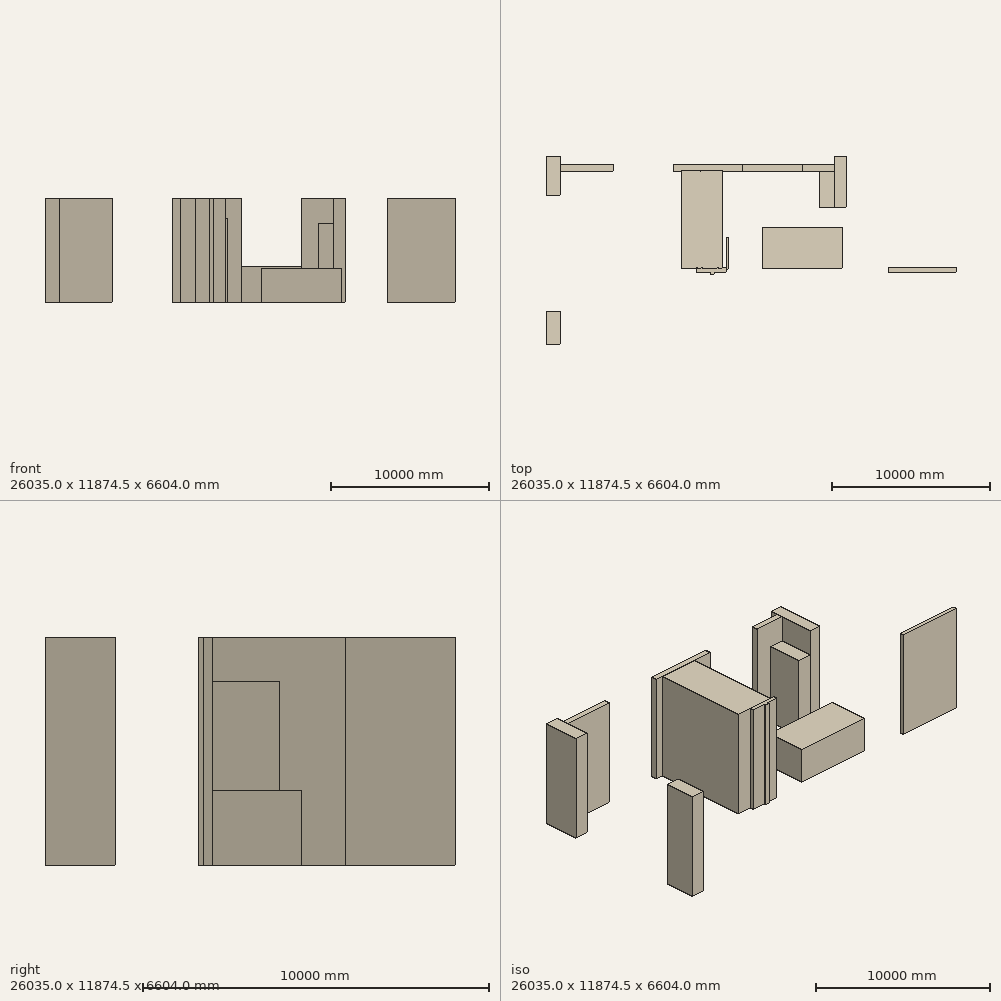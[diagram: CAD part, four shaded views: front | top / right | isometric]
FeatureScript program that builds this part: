
annotation { "Feature Type Name" : "Feature", "Feature Type Description" : "" }
export const myFeature = defineFeature(function(context is Context, id is Id, definition is map)
    precondition{}
    {
        {
            var Q0;
            Q0=qCreatedBy(makeId("Top.planeOp"),FACE);
            var sketch = newSketch(context, id + "F0", { "sketchPlane" : qUnion([Q0])});
            skLineSegment(sketch, "E0.bottom", {"start": v(0, 0) * mm, "end": v(762, 0) * mm});
            skLineSegment(sketch, "E0.top", {"start": v(0, -3175) * mm, "end": v(762, -3175) * mm});
            skLineSegment(sketch, "E0.left", {"start": v(0, 0) * mm, "end": v(0, -3175) * mm});
            skLineSegment(sketch, "E0.right", {"start": v(762, 0) * mm, "end": v(762, -3175) * mm});
            skLineSegment(sketch, "E1.bottom", {"start": v(0, -508) * mm, "end": v(-17399, -508) * mm});
            skLineSegment(sketch, "E1.top", {"start": v(0, -889) * mm, "end": v(-431.8, -889) * mm});
            skLineSegment(sketch, "E1.left", {"start": v(0, -508) * mm, "end": v(0, -889) * mm});
            skLineSegment(sketch, "E1.right", {"start": v(-17399, -508) * mm, "end": v(-17399, -889) * mm});
            skLineSegment(sketch, "E2.bottom", {"start": v(762, -3175) * mm, "end": v(508, -3175) * mm});
            skLineSegment(sketch, "E2.top", {"start": v(762, -7048.5) * mm, "end": v(508, -7048.5) * mm});
            skLineSegment(sketch, "E2.left", {"start": v(762, -3175) * mm, "end": v(762, -7048.5) * mm});
            skLineSegment(sketch, "E2.right", {"start": v(508, -4762.5) * mm, "end": v(508, -7048.5) * mm});
            skLineSegment(sketch, "E3.bottom", {"start": v(-17399, 0) * mm, "end": v(-18288, 0) * mm});
            skLineSegment(sketch, "E3.top", {"start": v(-17399, -2413) * mm, "end": v(-18288, -2413) * mm});
            skLineSegment(sketch, "E3.left", {"start": v(-17399, 0) * mm, "end": v(-17399, -2413) * mm});
            skLineSegment(sketch, "E3.right", {"start": v(-18288, 0) * mm, "end": v(-18288, -2413) * mm});
            skLineSegment(sketch, "E4.bottom", {"start": v(-18288, -2413) * mm, "end": v(-17907, -2413) * mm});
            skLineSegment(sketch, "E4.top", {"start": v(-18288, -9842.5) * mm, "end": v(-17907, -9842.5) * mm});
            skLineSegment(sketch, "E4.left", {"start": v(-18288, -2413) * mm, "end": v(-18288, -9842.5) * mm});
            skLineSegment(sketch, "E4.right", {"start": v(-17907, -2413) * mm, "end": v(-17907, -9842.5) * mm});
            skLineSegment(sketch, "E5.bottom", {"start": v(-18288, -9842.5) * mm, "end": v(-17399, -9842.5) * mm});
            skLineSegment(sketch, "E5.top", {"start": v(-18288, -11874.5) * mm, "end": v(-17399, -11874.5) * mm});
            skLineSegment(sketch, "E5.left", {"start": v(-18288, -9842.5) * mm, "end": v(-18288, -11874.5) * mm});
            skLineSegment(sketch, "E5.right", {"start": v(-17399, -9842.5) * mm, "end": v(-17399, -11874.5) * mm});
            skLineSegment(sketch, "E6.bottom", {"start": v(-7614.3, -7048.5) * mm, "end": v(7747, -7048.5) * mm});
            skLineSegment(sketch, "E6.top", {"start": v(-7614.3, -7302.5) * mm, "end": v(7747, -7302.5) * mm});
            skLineSegment(sketch, "E6.right", {"start": v(7747, -7048.5) * mm, "end": v(7747, -7302.5) * mm});
            skLineSegment(sketch, "E7.top", {"start": v(-7614.3, -9842.5) * mm, "end": v(7747, -9842.5) * mm});
            skLineSegment(sketch, "E7.left", {"start": v(-7614.3, -7302.5) * mm, "end": v(-7614.3, -9842.5) * mm});
            skLineSegment(sketch, "E7.right", {"start": v(7747, -7302.5) * mm, "end": v(7747, -9842.5) * mm});
            skLineSegment(sketch, "E8.bottom", {"start": v(-5588, -9842.5) * mm, "end": v(1016, -9842.5) * mm});
            skLineSegment(sketch, "E8.top", {"start": v(-4826, -10604.5) * mm, "end": v(1016, -10604.5) * mm});
            skLineSegment(sketch, "E8.left", {"start": v(-5588, -9842.5) * mm, "end": v(-5588, -10604.5) * mm});
            skLineSegment(sketch, "E8.right", {"start": v(1016, -9842.5) * mm, "end": v(1016, -10604.5) * mm});
            skLineSegment(sketch, "E9.top", {"start": v(-5588, -15303.5) * mm, "end": v(-4826, -15303.5) * mm});
            skLineSegment(sketch, "E9.left", {"start": v(-5588, -10604.5) * mm, "end": v(-5588, -15303.5) * mm});
            skLineSegment(sketch, "E9.right", {"start": v(-4826, -10604.5) * mm, "end": v(-4826, -15303.5) * mm});
            skLineSegment(sketch, "E10", {"start": v(-5588, -9842.5) * mm, "end": v(-17907, -9842.5) * mm});
            skLineSegment(sketch, "E11.top", {"start": v(-5588, -10096.5) * mm, "end": v(-7874, -10096.5) * mm});
            skLineSegment(sketch, "E11.left", {"start": v(-5588, -9842.5) * mm, "end": v(-5588, -10096.5) * mm});
            skLineSegment(sketch, "E12.bottom", {"start": v(-17907, -9842.5) * mm, "end": v(-7874, -9842.5) * mm});
            skLineSegment(sketch, "E12.top", {"start": v(-17907, -9588.5) * mm, "end": v(-7874, -9588.5) * mm});
            skLineSegment(sketch, "E12.left", {"start": v(-17907, -9842.5) * mm, "end": v(-17907, -9588.5) * mm});
            skLineSegment(sketch, "E12.right", {"start": v(-7874, -9842.5) * mm, "end": v(-7874, -9588.5) * mm});
            skLineSegment(sketch, "E13.bottom", {"start": v(-5588, -10096.5) * mm, "end": v(-5842, -10096.5) * mm});
            skLineSegment(sketch, "E13.top", {"start": v(-5588, -9842.5) * mm, "end": v(-5842, -9842.5) * mm});
            skLineSegment(sketch, "E13.left", {"start": v(-5588, -10096.5) * mm, "end": v(-5588, -9842.5) * mm});
            skLineSegment(sketch, "E13.right", {"start": v(-5842, -10096.5) * mm, "end": v(-5842, -9842.5) * mm});
            skLineSegment(sketch, "E14.bottom", {"start": v(-5842, -9842.5) * mm, "end": v(-7620, -9842.5) * mm});
            skLineSegment(sketch, "E14.top", {"start": v(-5842, -10096.5) * mm, "end": v(-7620, -10096.5) * mm});
            skLineSegment(sketch, "E14.left", {"start": v(-5842, -9842.5) * mm, "end": v(-5842, -10096.5) * mm});
            skLineSegment(sketch, "E14.right", {"start": v(-7620, -9842.5) * mm, "end": v(-7620, -10096.5) * mm});
            skLineSegment(sketch, "E15.bottom", {"start": v(-7620, -9842.5) * mm, "end": v(-7874, -9842.5) * mm});
            skLineSegment(sketch, "E15.top", {"start": v(-7620, -10096.5) * mm, "end": v(-7874, -10096.5) * mm});
            skLineSegment(sketch, "E15.right", {"start": v(-7874, -9842.5) * mm, "end": v(-7874, -10096.5) * mm});
            skLineSegment(sketch, "E16.bottom", {"start": v(-7874, -9842.5) * mm, "end": v(-7614.3, -9842.5) * mm});
            skLineSegment(sketch, "E16.top", {"start": v(-7874, -9461.5) * mm, "end": v(-7614.3, -9461.5) * mm});
            skLineSegment(sketch, "E16.left", {"start": v(-7874, -9842.5) * mm, "end": v(-7874, -9461.5) * mm});
            skLineSegment(sketch, "E16.right", {"start": v(-7614.3, -9842.5) * mm, "end": v(-7614.3, -9461.5) * mm});
            skLineSegment(sketch, "E17.left", {"start": v(-7874, -9461.5) * mm, "end": v(-7874, -7302.5) * mm});
            skLineSegment(sketch, "E17.right", {"start": v(-7614.3, -9461.5) * mm, "end": v(-7614.3, -7302.5) * mm});
            skLineSegment(sketch, "E18.top", {"start": v(-7874, -7429.5) * mm, "end": v(-7614.3, -7429.5) * mm});
            skLineSegment(sketch, "E18.left", {"start": v(-7874, -7302.5) * mm, "end": v(-7874, -7429.5) * mm});
            skLineSegment(sketch, "E18.right", {"start": v(-7614.3, -7302.5) * mm, "end": v(-7614.3, -7429.5) * mm});
            skLineSegment(sketch, "E19.bottom", {"start": v(-14033.5, -508) * mm, "end": v(-10223.5, -508) * mm});
            skLineSegment(sketch, "E19.top", {"start": v(-14033.5, -889) * mm, "end": v(-10223.5, -889) * mm});
            skLineSegment(sketch, "E19.left", {"start": v(-14033.5, -508) * mm, "end": v(-14033.5, -889) * mm});
            skLineSegment(sketch, "E19.right", {"start": v(-10223.5, -508) * mm, "end": v(-10223.5, -889) * mm});
            skLineSegment(sketch, "E20.bottom", {"start": v(-5842, -508) * mm, "end": v(-2032, -508) * mm});
            skLineSegment(sketch, "E20.top", {"start": v(-5842, -889) * mm, "end": v(-5080, -889) * mm});
            skLineSegment(sketch, "E20.left", {"start": v(-5842, -508) * mm, "end": v(-5842, -889) * mm});
            skLineSegment(sketch, "E20.right", {"start": v(-2032, -508) * mm, "end": v(-2032, -889) * mm});
            skLineSegment(sketch, "E21.bottom", {"start": v(-9715.5, -889) * mm, "end": v(-7106.3, -889) * mm});
            skLineSegment(sketch, "E21.top", {"start": v(-9715.5, -7048.5) * mm, "end": v(-7106.3, -7048.5) * mm});
            skLineSegment(sketch, "E21.left", {"start": v(-9715.5, -889) * mm, "end": v(-9715.5, -7048.5) * mm});
            skLineSegment(sketch, "E21.right", {"start": v(-7106.3, -889) * mm, "end": v(-7106.3, -7048.5) * mm});
            skLineSegment(sketch, "E22.bottom", {"start": v(-7874, -7302.5) * mm, "end": v(-8763, -7302.5) * mm});
            skLineSegment(sketch, "E22.top", {"start": v(-7874, -7048.5) * mm, "end": v(-8763, -7048.5) * mm});
            skLineSegment(sketch, "E22.right", {"start": v(-8763, -7302.5) * mm, "end": v(-8763, -7048.5) * mm});
            skLineSegment(sketch, "E23.bottom", {"start": v(508, -3175) * mm, "end": v(0, -3175) * mm});
            skLineSegment(sketch, "E23.left", {"start": v(508, -3175) * mm, "end": v(508, -4762.5) * mm});
            skLineSegment(sketch, "E24.top", {"start": v(508, -7048.5) * mm, "end": v(-431.8, -7048.5) * mm});
            skLineSegment(sketch, "E25.right", {"start": v(508, -4762.5) * mm, "end": v(508, -3517.9) * mm});
            skLineSegment(sketch, "E26.left", {"start": v(0, -889) * mm, "end": v(0, -3175) * mm});
            skLineSegment(sketch, "E27.bottom", {"start": v(-7106.3, -7048.5) * mm, "end": v(-4515.5, -7048.5) * mm, "construction": true});
            skLineSegment(sketch, "E28.bottom", {"start": v(-5836.3, -7048.5) * mm, "end": v(-3245.5, -7048.5) * mm});
            skLineSegment(sketch, "E29.left", {"start": v(0, -3175) * mm, "end": v(0, -889) * mm});
            skLineSegment(sketch, "E29.right", {"start": v(-431.8, -3175) * mm, "end": v(-431.8, -3129.28) * mm});
            skLineSegment(sketch, "E30.bottom", {"start": v(-431.8, -889) * mm, "end": v(0, -889) * mm});
            skLineSegment(sketch, "E30.left", {"start": v(-431.8, -889) * mm, "end": v(-431.8, -934.72) * mm});
            skLineSegment(sketch, "E30.right", {"start": v(0, -889) * mm, "end": v(0, -934.72) * mm});
            skLineSegment(sketch, "E31.right", {"start": v(0, -3175) * mm, "end": v(0, -3175) * mm});
            skLineSegment(sketch, "E32.trimOffspring", {"start": v(-5080, -889) * mm, "end": v(-17399, -889) * mm});
            skLineSegment(sketch, "E33.trimOffspring", {"start": v(-1574.8, -889) * mm, "end": v(-5080, -889) * mm});
            skLineSegment(sketch, "E34.bottom", {"start": v(-5842, -508) * mm, "end": v(0, -508) * mm});
            skLineSegment(sketch, "E34.top", {"start": v(-5842, -889) * mm, "end": v(0, -889) * mm});
            skLineSegment(sketch, "E35.top", {"start": v(-635, -5092.7) * mm, "end": v(-749.3, -5092.7) * mm});
            skLineSegment(sketch, "E36.bottom", {"start": v(1397, -7048.5) * mm, "end": v(3429, -7048.5) * mm});
            skLineSegment(sketch, "E36.top", {"start": v(1397, -7302.5) * mm, "end": v(3429, -7302.5) * mm});
            skLineSegment(sketch, "E36.left", {"start": v(1397, -7048.5) * mm, "end": v(1397, -7302.5) * mm});
            skLineSegment(sketch, "E36.right", {"start": v(3429, -7048.5) * mm, "end": v(3429, -7302.5) * mm});
            skLineSegment(sketch, "E37.bottom", {"start": v(-6852.3, -7048.5) * mm, "end": v(-4820.3, -7048.5) * mm});
            skLineSegment(sketch, "E37.top", {"start": v(-6852.3, -7302.5) * mm, "end": v(-4820.3, -7302.5) * mm});
            skLineSegment(sketch, "E37.left", {"start": v(-6852.3, -7048.5) * mm, "end": v(-6852.3, -7302.5) * mm});
            skLineSegment(sketch, "E37.right", {"start": v(-4820.3, -7048.5) * mm, "end": v(-4820.3, -7302.5) * mm});
            skLineSegment(sketch, "E38.bottom", {"start": v(-6852.3, -7137.4) * mm, "end": v(-6738, -7137.4) * mm});
            skLineSegment(sketch, "E38.top", {"start": v(-6852.3, -5105.4) * mm, "end": v(-6738, -5105.4) * mm});
            skLineSegment(sketch, "E38.left", {"start": v(-6852.3, -7137.4) * mm, "end": v(-6852.3, -5105.4) * mm});
            skLineSegment(sketch, "E38.right", {"start": v(-6738, -7137.4) * mm, "end": v(-6738, -5105.4) * mm});
            skLineSegment(sketch, "E39.trimOffspring", {"start": v(-5080, -1968.5) * mm, "end": v(-4515.5, -1968.5) * mm, "construction": true});
            skPoint(sketch, "E40.orphan", {"position": v(-3245.5, -1968.5) * mm});
            skLineSegment(sketch, "E41.trimOffspring", {"start": v(-431.8, -934.72) * mm, "end": v(-431.8, -889) * mm});
            skLineSegment(sketch, "E42.bottom", {"start": v(-4572, -7048.5) * mm, "end": v(508, -7048.5) * mm});
            skLineSegment(sketch, "E42.top", {"start": v(-4572, -4457.7) * mm, "end": v(508, -4457.7) * mm});
            skLineSegment(sketch, "E42.left", {"start": v(-4572, -7048.5) * mm, "end": v(-4572, -4457.7) * mm});
            skLineSegment(sketch, "E42.right", {"start": v(508, -7048.5) * mm, "end": v(508, -4457.7) * mm});
            skLineSegment(sketch, "E43.bottom", {"start": v(0, -889) * mm, "end": v(-939.8, -889) * mm});
            skLineSegment(sketch, "E43.top", {"start": v(0, -3175) * mm, "end": v(-939.8, -3175) * mm});
            skLineSegment(sketch, "E43.right", {"start": v(-939.8, -889) * mm, "end": v(-939.8, -3175) * mm});
            skSolve(sketch);
        }
        {
            var Q0;
            {var subQ3=sQuery(id+"F0.wireOp",EDGE,"E3.bottom");Q0=makeQuery(id+"F0.imprint","IMPRINT",FACE,{"disambiguationData":[TD([[makeQuery(id+"F0.imprint","IMPRINT",EDGE,{"derivedFrom":subQ3}),1.0]])]});}
            var Q1;
            {var subQ1=sQuery(id+"F0.wireOp",EDGE,"E5.bottom");Q1=makeQuery(id+"F0.imprint","IMPRINT",FACE,{"disambiguationData":[TD([[makeQuery(id+"F0.imprint","IMPRINT",EDGE,{"derivedFrom":subQ1}),-1.0]])]});}
            var Q2;
            Q2=makeQuery(id+"F0.imprint","IMPRINT",FACE,{"disambiguationData":[TD([[makeQuery(id+"F0.imprint","IMPRINT",EDGE,{"derivedFrom":sQuery(id+"F0.wireOp",EDGE,"E8.bottom")}),-1.0]])]});
            var Q3;
            Q3=makeQuery(id+"F0.imprint","IMPRINT",FACE,{"disambiguationData":[TD([[makeQuery(id+"F0.imprint","IMPRINT",EDGE,{"derivedFrom":sQuery(id+"F0.wireOp",EDGE,"E0.bottom")}),-1.0]])]});
            extrude(context, id + "F1", {"entities" : qUnion([Q0, Q1, Q2, Q3]), "depth" : 6604 * mm});
        }
        {
            var Q0;
            {var subQ3=sQuery(id+"F0.wireOp",EDGE,"E19.left");Q0=makeQuery(id+"F0.imprint","IMPRINT",FACE,{"disambiguationData":[TD([[makeQuery(id+"F0.imprint","IMPRINT",EDGE,{"derivedFrom":subQ3}),-1.0]])]});}
            var Q1;
            {var subQ4=sQuery(id+"F0.wireOp",EDGE,"E19.right");Q1=makeQuery(id+"F0.imprint","IMPRINT",FACE,{"disambiguationData":[TD([[makeQuery(id+"F0.imprint","IMPRINT",EDGE,{"derivedFrom":subQ4}),1.0]])]});}
            var Q2;
            {var subQ2=sQuery(id+"F0.wireOp",EDGE,"E20.right");Q2=makeQuery(id+"F0.imprint","IMPRINT",FACE,{"disambiguationData":[TD([[makeQuery(id+"F0.imprint","IMPRINT",EDGE,{"derivedFrom":subQ2}),1.0]])]});}
            var Q3;
            Q3=makeQuery(id+"F0.imprint","IMPRINT",FACE,{"disambiguationData":[TD([[makeQuery(id+"F0.imprint","IMPRINT",EDGE,{"derivedFrom":sQuery(id+"F0.wireOp",EDGE,"E2.bottom")}),1.0]])]});
            var Q4;
            {var subQ3=sQuery(id+"F0.wireOp",EDGE,"E16.right");Q4=makeQuery(id+"F0.imprint","IMPRINT",FACE,{"disambiguationData":[TD([[makeQuery(id+"F0.imprint","IMPRINT",EDGE,{"derivedFrom":subQ3}),1.0]])]});}
            var Q5;
            Q5=makeQuery(id+"F0.imprint","IMPRINT",FACE,{"disambiguationData":[TD([[makeQuery(id+"F0.imprint","IMPRINT",EDGE,{"derivedFrom":sQuery(id+"F0.wireOp",EDGE,"E15.top")}),-1.0]])]});
            var Q6;
            Q6=makeQuery(id+"F0.imprint","IMPRINT",FACE,{"disambiguationData":[TD([[makeQuery(id+"F0.imprint","IMPRINT",EDGE,{"derivedFrom":sQuery(id+"F0.wireOp",EDGE,"E13.bottom")}),-1.0]])]});
            extrude(context, id + "F2", {"entities" : qUnion([Q0, Q1, Q2, Q3, Q4, Q5, Q6]), "depth" : 6604 * mm});
        }
        {
            var Q0;
            Q0=makeQuery(id+"F0.imprint","IMPRINT",FACE,{"disambiguationData":[TD([[makeQuery(id+"F0.imprint","IMPRINT",EDGE,{"derivedFrom":sQuery(id+"F0.wireOp",EDGE,"E19.bottom")}),-1.0]])]});
            var Q1;
            {var subQ1=sQuery(id+"F0.wireOp",EDGE,"E20.right");Q1=makeQuery(id+"F0.imprint","IMPRINT",FACE,{"disambiguationData":[TD([[makeQuery(id+"F0.imprint","IMPRINT",EDGE,{"derivedFrom":subQ1}),-1.0]])]});}
            extrude(context, id + "F3", {"entities" : qUnion([Q0, Q1]), "depth" : 2286 * mm});
        }
        {
            var Q0;
            {var subQ0=sQuery(id+"F0.wireOp",EDGE,"E21.left");Q0=makeQuery(id+"F0.imprint","IMPRINT",FACE,{"disambiguationData":[TD([[makeQuery(id+"F0.imprint","IMPRINT",EDGE,{"derivedFrom":subQ0}),1.0]])]});}
            extrude(context, id + "F4", {"entities" : qUnion([Q0]), "depth" : 6604 * mm});
        }
        {
            var Q0;
            Q0=makeQuery(id+"F0.imprint","IMPRINT",FACE,{"disambiguationData":[TD([[makeQuery(id+"F0.imprint","IMPRINT",EDGE,{"derivedFrom":sQuery(id+"F0.wireOp",EDGE,"E18.top")}),1.0]])]});
            var Q1;
            {var subQ0=sQuery(id+"F0.wireOp",EDGE,"E28.bottom");Q1=makeQuery(id+"F0.imprint","IMPRINT",FACE,{"disambiguationData":[TD([[makeQuery(id+"F0.imprint","IMPRINT",EDGE,{"derivedFrom":subQ0}),-1.0]])]});}
            var Q2;
            {var subQ0=sQuery(id+"F0.wireOp",EDGE,"E6.right");Q2=makeQuery(id+"F0.imprint","IMPRINT",FACE,{"disambiguationData":[TD([[makeQuery(id+"F0.imprint","IMPRINT",EDGE,{"derivedFrom":subQ0}),-1.0]])]});}
            extrude(context, id + "F5", {"entities" : qUnion([Q0, Q1, Q2]), "depth" : 6604 * mm});
        }
        {
            var Q0;
            {var subQ5=sQuery(id+"F0.wireOp",EDGE,"E38.top");Q0=makeQuery(id+"F0.imprint","IMPRINT",FACE,{"disambiguationData":[TD([[makeQuery(id+"F0.imprint","IMPRINT",EDGE,{"derivedFrom":subQ5}),-1.0]])]});}
            var Q1;
            {var subQ5=sQuery(id+"F0.wireOp",EDGE,"E38.bottom");Q1=makeQuery(id+"F0.imprint","IMPRINT",FACE,{"disambiguationData":[TD([[makeQuery(id+"F0.imprint","IMPRINT",EDGE,{"derivedFrom":subQ5}),1.0]])]});}
            extrude(context, id + "F6", {"entities" : qUnion([Q0, Q1]), "depth" : 5334 * mm});
        }
        {
            var Q0;
            {var subQ0=sQuery(id+"F0.wireOp",EDGE,"E42.top");Q0=makeQuery(id+"F0.imprint","IMPRINT",FACE,{"disambiguationData":[TD([[makeQuery(id+"F0.imprint","IMPRINT",EDGE,{"derivedFrom":subQ0}),-1.0]])]});}
            extrude(context, id + "F7", {"entities" : qUnion([Q0]), "depth" : 2159 * mm});
        }
        {
            var Q0;
            {var subQ2=sQuery(id+"F0.wireOp",EDGE,"E43.right");Q0=makeQuery(id+"F0.imprint","IMPRINT",FACE,{"disambiguationData":[TD([[makeQuery(id+"F0.imprint","IMPRINT",EDGE,{"derivedFrom":subQ2}),1.0]])]});}
            extrude(context, id + "F8", {"entities" : qUnion([Q0]), "depth" : 5003.8 * mm});
        }
    });
